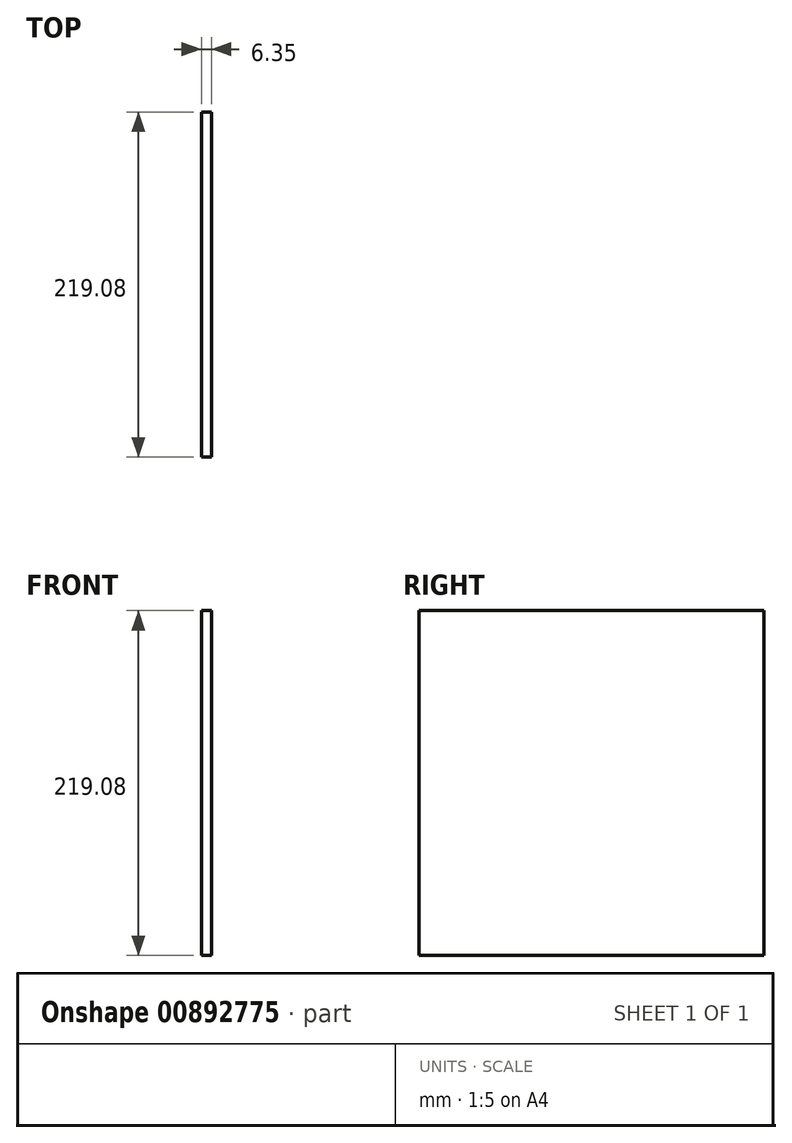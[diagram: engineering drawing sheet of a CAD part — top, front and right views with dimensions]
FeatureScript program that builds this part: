
annotation { "Feature Type Name" : "Feature", "Feature Type Description" : "" }
export const myFeature = defineFeature(function(context is Context, id is Id, definition is map)
    precondition{}
    {
        {
            var Q0;
            Q0=qCreatedBy(makeId("Right.planeOp"),FACE);
            var sketch = newSketch(context, id + "F0", { "sketchPlane" : qUnion([Q0])});
            skLineSegment(sketch, "E0.bottom", {"start": v(109.54, 109.54) * mm, "end": v(-109.54, 109.54) * mm});
            skLineSegment(sketch, "E0.top", {"start": v(109.54, -109.54) * mm, "end": v(-109.54, -109.54) * mm});
            skLineSegment(sketch, "E0.left", {"start": v(109.54, 109.54) * mm, "end": v(109.54, -109.54) * mm});
            skLineSegment(sketch, "E0.right", {"start": v(-109.54, 109.54) * mm, "end": v(-109.54, -109.54) * mm});
            skPoint(sketch, "E0.middle", {"position": v(0, 0) * mm});
            skSolve(sketch);
        }
        {
            var Q0;
            Q0 = qSketchRegion(id + "F0", true);
            extrude(context, id + "F1", {"entities" : qUnion([Q0]), "depth" : 6.35 * mm, "offsetDistance" : 25.4 * mm});
        }
    });
